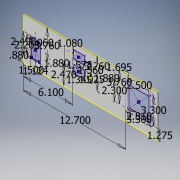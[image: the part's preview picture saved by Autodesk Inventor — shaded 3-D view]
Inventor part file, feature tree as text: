
AUTODESK INVENTOR PART (.ipt)
format: ipt  version: 2017 (Build 210142000, 142)  size: 220,160 bytes
history: native  units: in
note: dims shown in document units (in); Inventor stores cm internally (conversion verified against a paired STEP export)
features: extrude x4, hole x4, other x3, fillet x2, sketch x2
ambient origin geometry x8: Origin, YZ Plane, XZ Plane, XY Plane, X Axis, Y Axis, Z Axis, Center Point
bodies: Solid1 (feature_tree)
feature tree (15):
  extrude  "PDU back"  Depth=5.22in
  other  "pwr entry"
  extrude  "pwr entry cutout"  Depth=2.205in
  hole  "pwr entry holes"  [1 undecoded]
  other  "IEC outlet"
  hole  "IEC holes"  [1 undecoded]
  extrude  "IEC cutout"  Depth=0.196in
  other  "airflow"
  hole  "airflow holes"  [1 undecoded]
  extrude  "airflow cutout"  Depth=0.06in
  fillet  "IEC fillet 1"  [1 undecoded]
  fillet  "IEC fillet 2"  Radius=1.025in
  sketch  "Sketch5"  dims[d2=0.065in d3=0.0in d4=2.205in d5=1.124in d6=2.496in d7=1.5in d8=0.8795in d9=0.06in d10=0.0in d11=0.0in d12=0.136in d13=0.75in d14=0.375in d15=0.25in d16=0.5635in d17=1.0in d18=0.8108in d19=1.025in d20=1.345in d22=1.575in d23=6.1in d24=2.47in d25=0.7874in d27=1.56in d28=0.3937in d30=1.0in d34=0.136in d35=0.75in d36=0.375in d37=0.25in d38=0.5635in d39=1.0in d40=0.8108in d41=1.0in d42=0.0in d43=3.3in d44=3.3in d45=12.7in d46=1.275in d47=2.5in d48=2.81in d49=0.177in d50=0.75in d51=0.375in d52=0.25in d53=0.5635in d54=1.0in d55=0.8108in d56=1.0in d57=0.0in d58=0.196in d59=0.196in d60=2.3in d61=1.88in d62=1.08in d63=1.88in d64=1.695in d65=0.177in d66=0.75in d67=0.248in d68=0.25in d69=90.0deg d70=1.0in d71=0.8108in d73=3.76in d74=3.76in d75=3.76in]
  hole  "solid state relay holes"  [1 undecoded]
  sketch  "Sketch1"  dims[d0=16.73in d1=5.22in]
note: 5 required parameter values undecoded (feature->parameter linkage not recoverable at this tier; creation-order binding heuristic only, values carry confidence <= 0.55)
